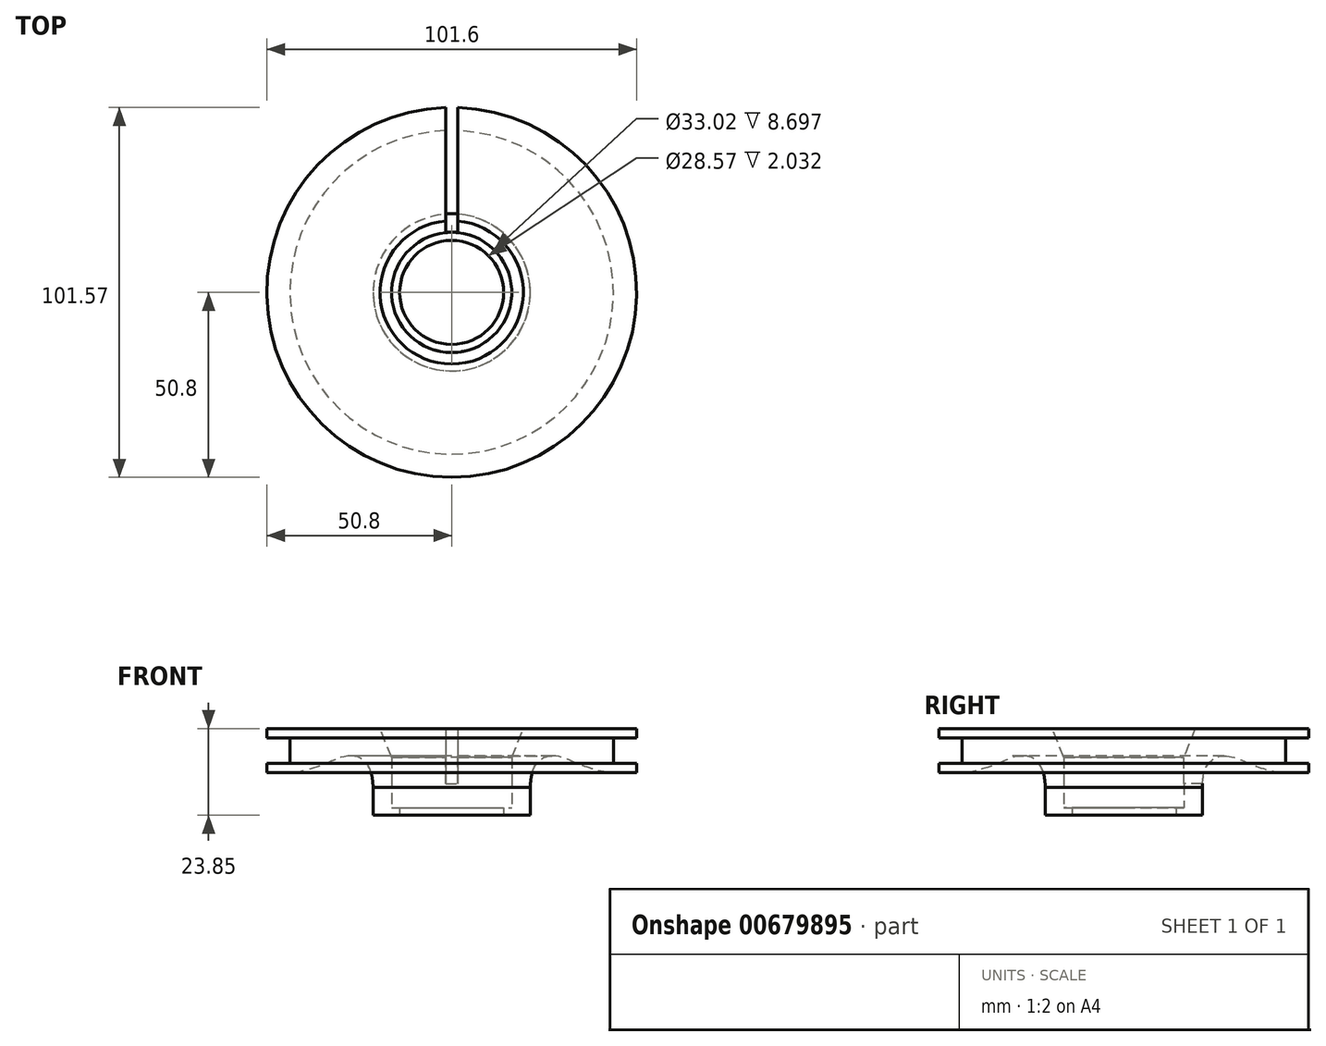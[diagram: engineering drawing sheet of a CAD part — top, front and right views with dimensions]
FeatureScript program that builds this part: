
annotation { "Feature Type Name" : "Feature", "Feature Type Description" : "" }
export const myFeature = defineFeature(function(context is Context, id is Id, definition is map)
    precondition{}
    {
        {
            var Q0;
            Q0=qCreatedBy(makeId("Front.planeOp"),FACE);
            var sketch = newSketch(context, id + "F0", { "sketchPlane" : qUnion([Q0])});
            skLineSegment(sketch, "E0.left", {"start": v(0, 101.61) * mm, "end": v(0, 144.88) * mm, "construction": true});
            skLineSegment(sketch, "E0.right", {"start": v(50.8, 87.99) * mm, "end": v(50.8, 90.53) * mm});
            skLineSegment(sketch, "E1", {"start": v(21.6, 76.2) * mm, "end": v(14.29, 76.2) * mm});
            skLineSegment(sketch, "E2", {"start": v(14.29, 76.2) * mm, "end": v(14.29, 78.23) * mm});
            skLineSegment(sketch, "E3", {"start": v(14.29, 78.23) * mm, "end": v(15.88, 78.23) * mm});
            skArc(sketch, "E4", {"start": v(16.51, 86.93) * mm, "mid": v(16.51, 86.95) * mm, "end": v(16.51, 86.96) * mm});
            skPoint(sketch, "E5.orphan", {"position": v(16.51, 86.96) * mm});
            skLineSegment(sketch, "E6", {"start": v(50.8, 87.99) * mm, "end": v(43.21, 87.99) * mm});
            skLineSegment(sketch, "E7", {"start": v(21.6, 76.2) * mm, "end": v(21.59, 83.91) * mm});
            skLineSegment(sketch, "E8", {"start": v(50.8, 90.53) * mm, "end": v(44.45, 90.53) * mm});
            skLineSegment(sketch, "E9", {"start": v(44.45, 90.53) * mm, "end": v(44.45, 97.51) * mm});
            skLineSegment(sketch, "E10", {"start": v(44.45, 97.51) * mm, "end": v(49.53, 97.51) * mm});
            skLineSegment(sketch, "E11", {"start": v(49.53, 100.05) * mm, "end": v(19.69, 100.05) * mm});
            skLineSegment(sketch, "E12", {"start": v(0, 52.41) * mm, "end": v(0, 130.74) * mm, "construction": true});
            skLineSegment(sketch, "E13", {"start": v(15.88, 78.23) * mm, "end": v(16.51, 78.23) * mm});
            skLineSegment(sketch, "E14", {"start": v(16.51, 86.93) * mm, "end": v(16.51, 78.23) * mm});
            skLineSegment(sketch, "E15", {"start": v(16.51, 86.93) * mm, "end": v(16.51, 92.08) * mm});
            skLineSegment(sketch, "E16", {"start": v(16.51, 92.08) * mm, "end": v(19.69, 100.05) * mm});
            skLineSegment(sketch, "E17", {"start": v(49.53, 97.51) * mm, "end": v(50.8, 97.51) * mm});
            skLineSegment(sketch, "E18", {"start": v(49.53, 100.05) * mm, "end": v(50.8, 100.05) * mm});
            skLineSegment(sketch, "E19.trimOffspring", {"start": v(50.8, 97.51) * mm, "end": v(50.8, 100.05) * mm});
            skFitSpline(sketch, "E20", {"points": [v(43.21, 87.99) * mm, v(40.05, 88.6) * mm, v(38.71, 88.95) * mm, v(36.48, 89.66) * mm, v(32.92, 91.1) * mm, v(30.33, 92.12) * mm, v(26.86, 92.47) * mm, v(24.32, 91.4) * mm, v(21.6, 83.91) * mm], "startDerivative": vector(-31.78, 0) * mm, "endDerivative": vector(-2.41, -70.16) * mm});
            skSolve(sketch);
        }
        {
            var Q0;
            Q0=makeQuery(id+"F0.imprint","IMPRINT",FACE,{"disambiguationData":[TD([[makeQuery(id+"F0.imprint","IMPRINT",EDGE,{"derivedFrom":sQuery(id+"F0.wireOp",EDGE,"E1")}),-1.0]])]});
            var Q1;
            Q1=sQuery(id+"F0.wireOp",EDGE,"E12");
            revolve(context, id + "F1", {"entities" : qUnion([Q0]), "axis" : qUnion([Q1]), "revolveType" : RevolveType.FULL});
        }
        {
            var Q0;
            Q0=qCreatedBy(makeId("Front.planeOp"),FACE);
            cPlane(context, id + "F2", {"entities" : qUnion([Q0]), "cplaneType" : CPlaneType.OFFSET, "offset" : 6.35 * mm, "oppositeDirection" : true, "width" : 152.4 * mm, "height" : 152.4 * mm});
        }
        {
            var Q0;
            Q0=qCreatedBy(id+"F2.planeOp",FACE);
            var sketch = newSketch(context, id + "F3", { "sketchPlane" : qUnion([Q0])});
            skLineSegment(sketch, "E21.bottom", {"start": v(-1.66, 84.84) * mm, "end": v(1.66, 84.84) * mm});
            skLineSegment(sketch, "E21.top", {"start": v(-1.66, 102.08) * mm, "end": v(1.66, 102.08) * mm});
            skLineSegment(sketch, "E21.left", {"start": v(-1.66, 84.84) * mm, "end": v(-1.66, 102.08) * mm});
            skLineSegment(sketch, "E21.right", {"start": v(1.66, 84.84) * mm, "end": v(1.66, 102.08) * mm});
            skSolve(sketch);
        }
        {
            var Q0;
            Q0=makeQuery(id+"F3.imprint","IMPRINT",FACE,{"disambiguationData":[TD([[makeQuery(id+"F3.imprint","IMPRINT",EDGE,{"derivedFrom":sQuery(id+"F3.wireOp",EDGE,"E21.bottom")}),1.0]])]});
            extrude(context, id + "F4", {"entities" : qUnion([Q0]), "operationType" : NewBodyOperationType.REMOVE, "oppositeDirection" : true, "depth" : 76.2 * mm, "offsetDistance" : 25.4 * mm});
        }
    });
